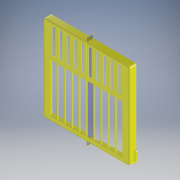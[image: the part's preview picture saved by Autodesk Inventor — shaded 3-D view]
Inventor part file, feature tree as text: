
AUTODESK INVENTOR PART (.ipt)
format: ipt  version: 2017 (Build 210142000, 142)  size: 830,976 bytes
history: native  units: mm
features: move_body x20, direct_edit x12, fillet x11, extrude x10, sketch x10, mirror x2, pattern_linear x2, plane x1, projected_geometry x1
ambient origin geometry x8: Origin, YZ Plane, XZ Plane, XY Plane, X Axis, Y Axis, Z Axis, Center Point
bodies: Solid1 (feature_tree)
feature tree (69):
  extrude  "Extrusion1"  Depth=90.0mm
  extrude  "Extrusion2"  Depth=3.0mm
  extrude  "Extrusion3"  Depth=3.0mm
  fillet  "Fillet1"  [1 undecoded]
  fillet  "Fillet2"  Radius=6.0mm
  extrude  "Extrusion4"  Depth=10.0mm
  direct_edit  "Direct Edit1"
  direct_edit  "Direct Edit2"
  direct_edit  "Direct Edit3"
  direct_edit  "Direct Edit4"
  extrude  "Extrusion5"  Depth=56.0mm
  fillet  "Fillet3"  Radius=86.0mm
  direct_edit  "Direct Edit5"
  extrude  "Extrusion6"  Depth=2.0mm TaperAngle=0.0deg
  direct_edit  "Direct Edit6"
  direct_edit  "Direct Edit7"
  direct_edit  "Direct Edit8"
  fillet  "Fillet4"  Radius=1.5mm
  fillet  "Fillet5"  Radius=4.0mm
  direct_edit  "Direct Edit9"
  direct_edit  "Direct Edit10"
  fillet  "Fillet6"  Radius=2.0mm
  extrude  "Extrusion7"  Depth=4.0mm
  fillet  "Fillet7"  Radius=4.0mm
  direct_edit  "Direct Edit12"
  direct_edit  "Direct Edit13"
  extrude  "Extrusion8"  TaperAngle=0.0deg  [1 undecoded]
  plane  "Work Plane1"
  mirror  "Mirror1"
  extrude  "Extrusion9"  TaperAngle=0.0deg  [1 undecoded]
  fillet  "Fillet10"  [1 undecoded]
  fillet  "Fillet11"  Radius=1.0mm
  fillet  "Fillet12"  Radius=3.0mm
  mirror  "Mirror2"
  extrude  "Extrusion10"  Depth=1.0mm TaperAngle=0.0deg
  pattern_linear  "Rectangular Pattern1"  Spacing1=87.0mm  [1 undecoded]
  pattern_linear  "Rectangular Pattern2"  Spacing1=1.0mm  [1 undecoded]
  fillet  "Fillet13"  Radius=1.0mm
  sketch  "Sketch1"  dims[d0=90.0mm d1=90.0mm]
  sketch  "Sketch2"  dims[d2=3.0mm d3=27.0mm]
  sketch  "Sketch3"  dims[d4=100.0mm d6=7.62mm d7=10.0mm d9=10.0mm d11=3.0mm d12=90.0deg d13=6.0mm]
  projected_geometry  "Projected Loop2"
  sketch  "Sketch4"  dims[d14=50.0mm d15=100.0mm d17=7.62mm d18=10.0mm d20=10.0mm]
  sketch  "Sketch6"  dims[d22=0.5mm d23=0.0mm d24=56.0mm d25=86.0mm]
  sketch  "Sketch7"  dims[d26=90.0deg d27=1.5mm d28=0.0mm d29=1.5mm d30=4.0mm d31=0.0mm d32=2.0mm]
  sketch  "Sketch8"  dims[d33=1.0mm d34=6.0mm d35=4.0mm]
  sketch  "Sketch10"  dims[d36=19.25mm d37=0.0mm d38=0.0mm d39=0.0mm d40=-10.0mm]
  sketch  "Sketch11"  dims[d41=0.0mm d42=0.0mm d43=5.5mm d44=0.0mm d45=0.0mm d46=-5.5mm]
  sketch  "Sketch12"  dims[d47=0.0mm d48=0.0mm d49=4.0mm d50=0.0mm d51=0.0mm d52=-2.5mm d53=1.0mm d54=0.0mm d55=3.0mm d56=0.0mm d57=0.0mm d58=0.5mm d61=87.0mm d62=1.0mm d63=1.0mm d64=1.0mm d65=20.0mm d66=0.5mm d67=0.0mm d68=0.0mm d69=0.0mm d70=1.0mm d71=0.0mm d72=0.0mm d73=0.5mm d74=0.0mm d75=0.0mm d76=25.0mm d77=0.0mm d78=0.0mm d79=-10.0mm d80=0.0mm d81=0.0mm d82=9.0mm d83=0.0mm d84=0.0mm d85=0.1mm d86=0.0mm d87=0.0mm d88=0.1mm d89=0.0mm d90=0.0mm d91=0.25mm d92=1.0mm d93=1.0mm d94=0.0mm d95=0.0mm d96=-0.25mm d97=0.0mm d98=0.0mm d99=0.75mm d100=0.0mm d101=0.0mm d102=-1.0mm d103=1.0mm d104=4.0mm d105=2.0mm d106=4.0mm d107=2.0mm d108=3.0mm d109=0.0mm d113=1.0mm d114=0.0mm d115=0.0mm d116=2.5mm d117=0.0mm d118=0.0mm d119=-1.75mm d120=0.0mm d121=0.0mm d122=-0.6mm d123=3.5mm d124=12.0mm d125=1.5mm d126=0.0mm d129=14.0mm d130=4.0mm d131=2.0mm d132=0.0mm d133=1.0mm d134=2.0mm d135=5.0mm d140=2.0mm d141=-3.490659mm d142=100.0mm d144=7.6mm d145=20.0mm d147=25.0mm d148=1.0mm]
  move_body  "Move1"
  move_body  "Move2"
  move_body  "Move3"
  move_body  "Move4"
  move_body  "Move5"
  move_body  "Move6"
  move_body  "Move7"
  move_body  "Move8"
  move_body  "Move9"
  move_body  "Move10"
  move_body  "Move11"
  move_body  "Move12"
  move_body  "Move13"
  move_body  "Move14"
  move_body  "Move15"
  move_body  "Move16"
  move_body  "Move17"
  move_body  "Move19"
  move_body  "Move20"
  move_body  "Move21"
note: 6 required parameter values undecoded (feature->parameter linkage not recoverable at this tier; creation-order binding heuristic only, values carry confidence <= 0.55)
